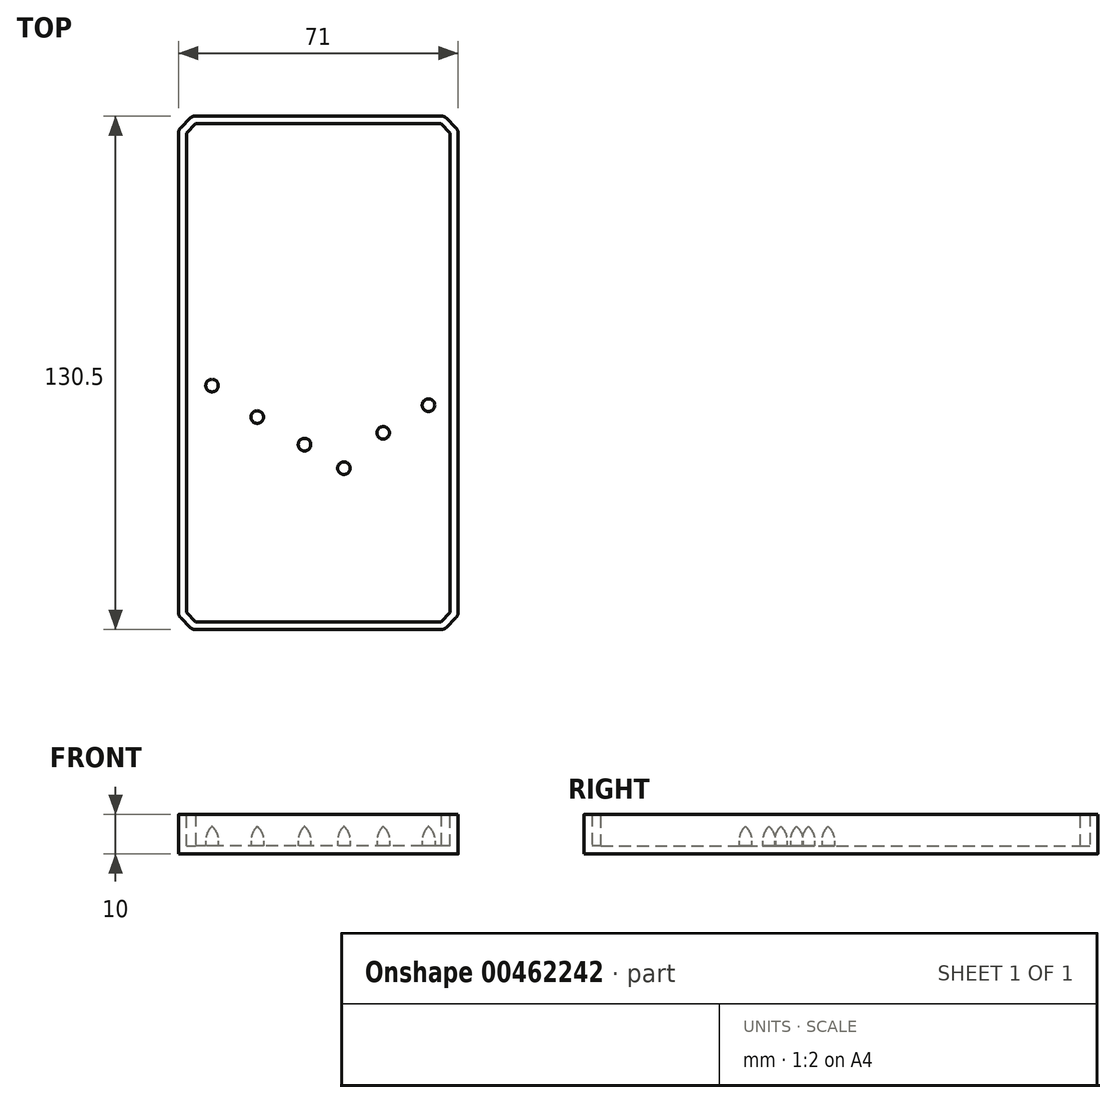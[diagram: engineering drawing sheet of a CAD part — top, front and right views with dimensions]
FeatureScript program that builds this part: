
annotation { "Feature Type Name" : "Feature", "Feature Type Description" : "" }
export const myFeature = defineFeature(function(context is Context, id is Id, definition is map)
    precondition{}
    {
        {
            var Q0;
            Q0=qCreatedBy(makeId("Top.planeOp"),FACE);
            var sketch = newSketch(context, id + "F0", { "sketchPlane" : qUnion([Q0])});
            skLineSegment(sketch, "E0.bottom", {"start": v(35.5, -65.25) * mm, "end": v(-35.5, -65.25) * mm});
            skLineSegment(sketch, "E0.top", {"start": v(35.5, 65.25) * mm, "end": v(-35.5, 65.25) * mm});
            skLineSegment(sketch, "E0.left", {"start": v(35.5, -65.25) * mm, "end": v(35.5, 65.25) * mm});
            skLineSegment(sketch, "E0.right", {"start": v(-35.5, -65.25) * mm, "end": v(-35.5, 65.25) * mm});
            skPoint(sketch, "E0.middle", {"position": v(0, 0) * mm});
            skSolve(sketch);
        }
        {
            var Q0;
            Q0=qSketchRegion(id+"F0",true);
            extrude(context, id + "F1", {"entities" : qUnion([Q0]), "depth" : 10 * mm});
        }
        {
            var Q0;
            Q0=makeQuery(id+"F1.opExtrude","SWEPT_EDGE",EDGE,{"disambiguationData":[OSD([sQuery(id+"F0.wireOp",EDGE,"E0.bottom"),sQuery(id+"F0.wireOp",EDGE,"E0.right")])]});
            var Q1;
            Q1=makeQuery(id+"F1.opExtrude","SWEPT_EDGE",EDGE,{"disambiguationData":[OSD([sQuery(id+"F0.wireOp",EDGE,"E0.bottom"),sQuery(id+"F0.wireOp",EDGE,"E0.left")])]});
            var Q2;
            Q2=makeQuery(id+"F1.opExtrude","SWEPT_EDGE",EDGE,{"disambiguationData":[OSD([sQuery(id+"F0.wireOp",EDGE,"E0.top"),sQuery(id+"F0.wireOp",EDGE,"E0.right")])]});
            var Q3;
            Q3=makeQuery(id+"F1.opExtrude","SWEPT_EDGE",EDGE,{"disambiguationData":[OSD([sQuery(id+"F0.wireOp",EDGE,"E0.top"),sQuery(id+"F0.wireOp",EDGE,"E0.left")])]});
            chamfer(context, id + "F2", {"entities" : qUnion([Q0, Q1, Q2, Q3]), "width" : 3.5 * mm, "tangentPropagation" : true});
        }
        {
            var Q0;
            {var subQ0=sQuery(id+"F0.wireOp",EDGE,"E0.top");Q0=makeQuery(id+"F2.opChamfer","BLEND_EDGE",EDGE,{"blendedFrom":[makeQuery(id+"F1.opExtrude","SWEPT_EDGE",EDGE,{"disambiguationData":[OSD([subQ0,sQuery(id+"F0.wireOp",EDGE,"E0.right")])]}),makeQuery(id+"F1.opExtrude","SWEPT_FACE",FACE,{"disambiguationData":[OSD([subQ0])]})],"blendedInto":[makeQuery(id+"F1.opExtrude","SWEPT_FACE",FACE,{"disambiguationData":[OSD([subQ0])]})]});}
            var Q1;
            {var subQ0=sQuery(id+"F0.wireOp",EDGE,"E0.right");Q1=makeQuery(id+"F2.opChamfer","BLEND_EDGE",EDGE,{"blendedFrom":[makeQuery(id+"F1.opExtrude","SWEPT_EDGE",EDGE,{"disambiguationData":[OSD([sQuery(id+"F0.wireOp",EDGE,"E0.top"),subQ0])]}),makeQuery(id+"F1.opExtrude","SWEPT_FACE",FACE,{"disambiguationData":[OSD([subQ0])]})],"blendedInto":[makeQuery(id+"F1.opExtrude","SWEPT_FACE",FACE,{"disambiguationData":[OSD([subQ0])]})]});}
            var Q2;
            {var subQ0=sQuery(id+"F0.wireOp",EDGE,"E0.top");Q2=makeQuery(id+"F2.opChamfer","BLEND_EDGE",EDGE,{"blendedFrom":[makeQuery(id+"F1.opExtrude","SWEPT_EDGE",EDGE,{"disambiguationData":[OSD([subQ0,sQuery(id+"F0.wireOp",EDGE,"E0.left")])]}),makeQuery(id+"F1.opExtrude","SWEPT_FACE",FACE,{"disambiguationData":[OSD([subQ0])]})],"blendedInto":[makeQuery(id+"F1.opExtrude","SWEPT_FACE",FACE,{"disambiguationData":[OSD([subQ0])]})]});}
            var Q3;
            {var subQ0=sQuery(id+"F0.wireOp",EDGE,"E0.left");Q3=makeQuery(id+"F2.opChamfer","BLEND_EDGE",EDGE,{"blendedFrom":[makeQuery(id+"F1.opExtrude","SWEPT_EDGE",EDGE,{"disambiguationData":[OSD([sQuery(id+"F0.wireOp",EDGE,"E0.top"),subQ0])]}),makeQuery(id+"F1.opExtrude","SWEPT_FACE",FACE,{"disambiguationData":[OSD([subQ0])]})],"blendedInto":[makeQuery(id+"F1.opExtrude","SWEPT_FACE",FACE,{"disambiguationData":[OSD([subQ0])]})]});}
            var Q4;
            {var subQ0=sQuery(id+"F0.wireOp",EDGE,"E0.bottom");Q4=makeQuery(id+"F2.opChamfer","BLEND_EDGE",EDGE,{"blendedFrom":[makeQuery(id+"F1.opExtrude","SWEPT_EDGE",EDGE,{"disambiguationData":[OSD([subQ0,sQuery(id+"F0.wireOp",EDGE,"E0.left")])]}),makeQuery(id+"F1.opExtrude","SWEPT_FACE",FACE,{"disambiguationData":[OSD([subQ0])]})],"blendedInto":[makeQuery(id+"F1.opExtrude","SWEPT_FACE",FACE,{"disambiguationData":[OSD([subQ0])]})]});}
            var Q5;
            {var subQ0=sQuery(id+"F0.wireOp",EDGE,"E0.left");Q5=makeQuery(id+"F2.opChamfer","BLEND_EDGE",EDGE,{"blendedFrom":[makeQuery(id+"F1.opExtrude","SWEPT_EDGE",EDGE,{"disambiguationData":[OSD([sQuery(id+"F0.wireOp",EDGE,"E0.bottom"),subQ0])]}),makeQuery(id+"F1.opExtrude","SWEPT_FACE",FACE,{"disambiguationData":[OSD([subQ0])]})],"blendedInto":[makeQuery(id+"F1.opExtrude","SWEPT_FACE",FACE,{"disambiguationData":[OSD([subQ0])]})]});}
            var Q6;
            {var subQ0=sQuery(id+"F0.wireOp",EDGE,"E0.right");Q6=makeQuery(id+"F2.opChamfer","BLEND_EDGE",EDGE,{"blendedFrom":[makeQuery(id+"F1.opExtrude","SWEPT_EDGE",EDGE,{"disambiguationData":[OSD([sQuery(id+"F0.wireOp",EDGE,"E0.bottom"),subQ0])]}),makeQuery(id+"F1.opExtrude","SWEPT_FACE",FACE,{"disambiguationData":[OSD([subQ0])]})],"blendedInto":[makeQuery(id+"F1.opExtrude","SWEPT_FACE",FACE,{"disambiguationData":[OSD([subQ0])]})]});}
            var Q7;
            {var subQ0=sQuery(id+"F0.wireOp",EDGE,"E0.bottom");Q7=makeQuery(id+"F2.opChamfer","BLEND_EDGE",EDGE,{"blendedFrom":[makeQuery(id+"F1.opExtrude","SWEPT_EDGE",EDGE,{"disambiguationData":[OSD([subQ0,sQuery(id+"F0.wireOp",EDGE,"E0.right")])]}),makeQuery(id+"F1.opExtrude","SWEPT_FACE",FACE,{"disambiguationData":[OSD([subQ0])]})],"blendedInto":[makeQuery(id+"F1.opExtrude","SWEPT_FACE",FACE,{"disambiguationData":[OSD([subQ0])]})]});}
            fillet(context, id + "F3", {"entities" : qUnion([Q0, Q1, Q2, Q3, Q4, Q5, Q6, Q7]), "radius" : 2 * mm, "tangentPropagation" : true, "allowEdgeOverflow" : false});
        }
        {
            var Q0;
            Q0=makeQuery(id+"F1.opExtrude","CAP_FACE",FACE,{"disambiguationData":[OSD([sQuery(id+"F0.wireOp",EDGE,"E0.bottom"),sQuery(id+"F0.wireOp",EDGE,"E0.top"),sQuery(id+"F0.wireOp",EDGE,"E0.left"),sQuery(id+"F0.wireOp",EDGE,"E0.right")])],"isStart":false});
            shell(context, id + "F4", {"entities" : qUnion([Q0]), "thickness" : 2 * mm});
        }
        {
            var Q0;
            Q0=makeQuery(id+"F4.opShell","OFFSET_FACE",FACE,{"disambiguationData":[OSD([sQuery(id+"F0.wireOp",EDGE,"E0.bottom"),sQuery(id+"F0.wireOp",EDGE,"E0.top"),sQuery(id+"F0.wireOp",EDGE,"E0.left"),sQuery(id+"F0.wireOp",EDGE,"E0.right")])]});
            var sketch = newSketch(context, id + "F5", { "sketchPlane" : qUnion([Q0])});
            skCircle(sketch, "E1", {"center": v(-27, -3.25) * mm, "radius": 1.6 * mm});
            skCircle(sketch, "E2", {"center": v(-15.5, -11.25) * mm, "radius": 1.6 * mm});
            skCircle(sketch, "E3", {"center": v(-3.5, -18.25) * mm, "radius": 1.6 * mm});
            skCircle(sketch, "E4", {"center": v(6.5, -24.25) * mm, "radius": 1.6 * mm});
            skCircle(sketch, "E5", {"center": v(16.5, -15.25) * mm, "radius": 1.6 * mm});
            skCircle(sketch, "E6", {"center": v(28, -8.25) * mm, "radius": 1.6 * mm});
            skSolve(sketch);
        }
        {
            var Q0;
            Q0 = qSketchRegion(id + "F5", true);
            extrude(context, id + "F6", {"entities" : qUnion([Q0]), "operationType" : NewBodyOperationType.ADD, "depth" : 5 * mm});
        }
        {
            var Q0;
            Q0=makeQuery(id+"F6.opExtrude","CAP_EDGE",EDGE,{"disambiguationData":[OSD([sQuery(id+"F5.wireOp",EDGE,"E1")])],"isStart":false});
            var Q1;
            Q1=makeQuery(id+"F6.opExtrude","CAP_EDGE",EDGE,{"disambiguationData":[OSD([sQuery(id+"F5.wireOp",EDGE,"E2")])],"isStart":false});
            var Q2;
            Q2=makeQuery(id+"F6.opExtrude","CAP_EDGE",EDGE,{"disambiguationData":[OSD([sQuery(id+"F5.wireOp",EDGE,"E3")])],"isStart":false});
            var Q3;
            Q3=makeQuery(id+"F6.opExtrude","CAP_EDGE",EDGE,{"disambiguationData":[OSD([sQuery(id+"F5.wireOp",EDGE,"E4")])],"isStart":false});
            var Q4;
            Q4=makeQuery(id+"F6.opExtrude","CAP_EDGE",EDGE,{"disambiguationData":[OSD([sQuery(id+"F5.wireOp",EDGE,"E5")])],"isStart":false});
            var Q5;
            Q5=makeQuery(id+"F6.opExtrude","CAP_EDGE",EDGE,{"disambiguationData":[OSD([sQuery(id+"F5.wireOp",EDGE,"E6")])],"isStart":false});
            chamfer(context, id + "F7", {"entities" : qUnion([Q0, Q1, Q2, Q3, Q4, Q5]), "width" : 1.6 * mm, "tangentPropagation" : true});
        }
        {
            var Q0;
            {var subQ0=sQuery(id+"F5.wireOp",EDGE,"E1");Q0=makeQuery(id+"F7.opChamfer","BLEND_EDGE",EDGE,{"blendedFrom":[makeQuery(id+"F6.opExtrude","CAP_EDGE",EDGE,{"disambiguationData":[OSD([subQ0])],"isStart":false}),makeQuery(id+"F6.opExtrude","SWEPT_FACE",FACE,{"disambiguationData":[OSD([subQ0])]})],"blendedInto":[makeQuery(id+"F6.opExtrude","SWEPT_FACE",FACE,{"disambiguationData":[OSD([subQ0])]})]});}
            var Q1;
            {var subQ0=sQuery(id+"F5.wireOp",EDGE,"E2");Q1=makeQuery(id+"F7.opChamfer","BLEND_EDGE",EDGE,{"blendedFrom":[makeQuery(id+"F6.opExtrude","CAP_EDGE",EDGE,{"disambiguationData":[OSD([subQ0])],"isStart":false}),makeQuery(id+"F6.opExtrude","SWEPT_FACE",FACE,{"disambiguationData":[OSD([subQ0])]})],"blendedInto":[makeQuery(id+"F6.opExtrude","SWEPT_FACE",FACE,{"disambiguationData":[OSD([subQ0])]})]});}
            var Q2;
            {var subQ0=sQuery(id+"F5.wireOp",EDGE,"E3");Q2=makeQuery(id+"F7.opChamfer","BLEND_EDGE",EDGE,{"blendedFrom":[makeQuery(id+"F6.opExtrude","CAP_EDGE",EDGE,{"disambiguationData":[OSD([subQ0])],"isStart":false}),makeQuery(id+"F6.opExtrude","SWEPT_FACE",FACE,{"disambiguationData":[OSD([subQ0])]})],"blendedInto":[makeQuery(id+"F6.opExtrude","SWEPT_FACE",FACE,{"disambiguationData":[OSD([subQ0])]})]});}
            var Q3;
            {var subQ0=sQuery(id+"F5.wireOp",EDGE,"E4");Q3=makeQuery(id+"F7.opChamfer","BLEND_EDGE",EDGE,{"blendedFrom":[makeQuery(id+"F6.opExtrude","CAP_EDGE",EDGE,{"disambiguationData":[OSD([subQ0])],"isStart":false}),makeQuery(id+"F6.opExtrude","SWEPT_FACE",FACE,{"disambiguationData":[OSD([subQ0])]})],"blendedInto":[makeQuery(id+"F6.opExtrude","SWEPT_FACE",FACE,{"disambiguationData":[OSD([subQ0])]})]});}
            var Q4;
            {var subQ0=sQuery(id+"F5.wireOp",EDGE,"E5");Q4=makeQuery(id+"F7.opChamfer","BLEND_EDGE",EDGE,{"blendedFrom":[makeQuery(id+"F6.opExtrude","CAP_EDGE",EDGE,{"disambiguationData":[OSD([subQ0])],"isStart":false}),makeQuery(id+"F6.opExtrude","SWEPT_FACE",FACE,{"disambiguationData":[OSD([subQ0])]})],"blendedInto":[makeQuery(id+"F6.opExtrude","SWEPT_FACE",FACE,{"disambiguationData":[OSD([subQ0])]})]});}
            var Q5;
            {var subQ0=sQuery(id+"F5.wireOp",EDGE,"E6");Q5=makeQuery(id+"F7.opChamfer","BLEND_EDGE",EDGE,{"blendedFrom":[makeQuery(id+"F6.opExtrude","CAP_EDGE",EDGE,{"disambiguationData":[OSD([subQ0])],"isStart":false}),makeQuery(id+"F6.opExtrude","SWEPT_FACE",FACE,{"disambiguationData":[OSD([subQ0])]})],"blendedInto":[makeQuery(id+"F6.opExtrude","SWEPT_FACE",FACE,{"disambiguationData":[OSD([subQ0])]})]});}
            fillet(context, id + "F8", {"entities" : qUnion([Q0, Q1, Q2, Q3, Q4, Q5]), "radius" : 5 * mm, "tangentPropagation" : true, "allowEdgeOverflow" : false});
        }
    });
